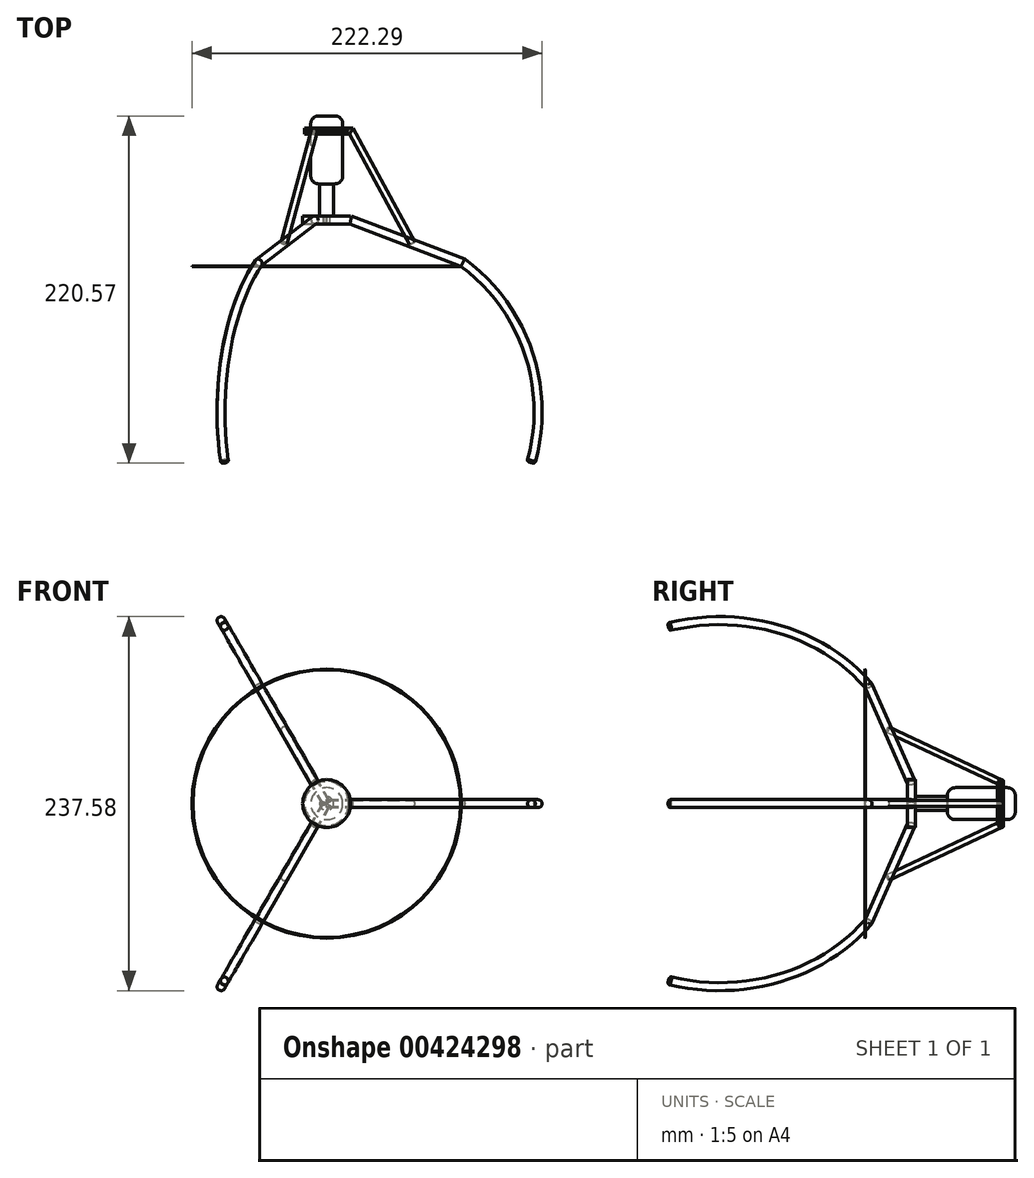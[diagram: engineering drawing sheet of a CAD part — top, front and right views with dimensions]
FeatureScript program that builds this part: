
annotation { "Feature Type Name" : "Feature", "Feature Type Description" : "" }
export const myFeature = defineFeature(function(context is Context, id is Id, definition is map)
    precondition{}
    {
        {
            var Q0;
            Q0=qCreatedBy(makeId("Top.planeOp"),FACE);
            var sketch = newSketch(context, id + "F0", { "sketchPlane" : qUnion([Q0])});
            skLineSegment(sketch, "E0.bottom", {"start": v(15.24, -2.54) * mm, "end": v(-15.24, -2.54) * mm});
            skLineSegment(sketch, "E0.top", {"start": v(15.24, 2.54) * mm, "end": v(-15.24, 2.54) * mm});
            skLineSegment(sketch, "E0.left", {"start": v(15.24, -2.54) * mm, "end": v(15.24, 2.54) * mm});
            skLineSegment(sketch, "E0.right", {"start": v(-15.24, -2.54) * mm, "end": v(-15.24, 2.54) * mm});
            skPoint(sketch, "E0.middle", {"position": v(0, 0) * mm});
            skLineSegment(sketch, "E1.bottom", {"start": v(4.45, 2.54) * mm, "end": v(-4.45, 2.54) * mm});
            skLineSegment(sketch, "E1.top", {"start": v(4.44, 22.86) * mm, "end": v(-4.45, 22.86) * mm});
            skLineSegment(sketch, "E1.left", {"start": v(4.45, 2.54) * mm, "end": v(4.44, 22.86) * mm});
            skLineSegment(sketch, "E1.right", {"start": v(-4.45, 2.54) * mm, "end": v(-4.45, 22.86) * mm});
            skPoint(sketch, "E1.middle", {"position": v(0, 12.7) * mm});
            skLineSegment(sketch, "E2.bottom", {"start": v(0, 22.86) * mm, "end": v(10.16, 22.86) * mm});
            skLineSegment(sketch, "E2.top", {"start": v(0, 66.04) * mm, "end": v(10.16, 66.04) * mm});
            skLineSegment(sketch, "E2.left", {"start": v(0, 22.86) * mm, "end": v(0, 66.04) * mm});
            skLineSegment(sketch, "E2.right", {"start": v(10.16, 22.86) * mm, "end": v(10.16, 66.04) * mm});
            skLineSegment(sketch, "E3.bottom", {"start": v(0, 22.86) * mm, "end": v(-10.16, 22.86) * mm});
            skLineSegment(sketch, "E3.top", {"start": v(0, 66.04) * mm, "end": v(-10.16, 66.04) * mm});
            skLineSegment(sketch, "E3.right", {"start": v(-10.16, 22.86) * mm, "end": v(-10.16, 66.04) * mm});
            skLineSegment(sketch, "E4.bottom", {"start": v(13.97, 54.57) * mm, "end": v(-13.97, 54.57) * mm});
            skLineSegment(sketch, "E4.top", {"start": v(13.97, 58.38) * mm, "end": v(-13.97, 58.38) * mm});
            skLineSegment(sketch, "E4.left", {"start": v(13.97, 54.57) * mm, "end": v(13.97, 58.38) * mm});
            skLineSegment(sketch, "E4.right", {"start": v(-13.97, 54.57) * mm, "end": v(-13.97, 58.38) * mm});
            skPoint(sketch, "E4.middle", {"position": v(0, 56.47) * mm});
            skArc(sketch, "E5", {"start": v(17.88, 57.68) * mm, "mid": v(16.1, 58.97) * mm, "end": v(13.97, 58.38) * mm});
            skArc(sketch, "E6", {"start": v(-13.97, 58.38) * mm, "mid": v(-18.2, 56.47) * mm, "end": v(-13.97, 54.57) * mm});
            skArc(sketch, "E7", {"start": v(16.15, 2.37) * mm, "mid": v(15.7, 2.5) * mm, "end": v(15.24, 2.54) * mm});
            skArc(sketch, "E8", {"start": v(-15.24, 2.54) * mm, "mid": v(-17.78, 0) * mm, "end": v(-15.24, -2.54) * mm});
            skLineSegment(sketch, "E9", {"start": v(17.88, 57.68) * mm, "end": v(56.07, -12.87) * mm});
            skLineSegment(sketch, "E10", {"start": v(13.42, 55.26) * mm, "end": v(48.8, -10.1) * mm});
            skLineSegment(sketch, "E11", {"start": v(16.15, 2.37) * mm, "end": v(48.8, -10.1) * mm});
            skLineSegment(sketch, "E12", {"start": v(14.77, -2.54) * mm, "end": v(85.52, -29.56) * mm});
            skArc(sketch, "E13", {"start": v(84.92, -29.23) * mm, "mid": v(85.2, -29.41) * mm, "end": v(85.52, -29.56) * mm});
            skArc(sketch, "E14", {"start": v(127.93, -151.04) * mm, "mid": v(129.74, -154.14) * mm, "end": v(132.84, -152.33) * mm});
            skArc(sketch, "E15", {"start": v(127.93, -151.04) * mm, "mid": v(125.12, -83.53) * mm, "end": v(84.92, -29.23) * mm});
            skArc(sketch, "E16", {"start": v(132.84, -152.33) * mm, "mid": v(129.91, -81.84) * mm, "end": v(87.93, -25.14) * mm});
            skLineSegment(sketch, "E17", {"start": v(0, -41.5) * mm, "end": v(0, 92.44) * mm});
            skLineSegment(sketch, "E18", {"start": v(44.62, -13.94) * mm, "end": v(59.96, -19.8) * mm});
            skPoint(sketch, "E19.trimOffspring.start.orphan", {"position": v(56.63, -13.94) * mm});
            skArc(sketch, "E20.trimOffspring", {"start": v(87.93, -25.14) * mm, "mid": v(87.65, -24.95) * mm, "end": v(87.33, -24.8) * mm});
            skLineSegment(sketch, "E21.trimOffspring", {"start": v(56.07, -12.87) * mm, "end": v(87.33, -24.8) * mm});
            skLineSegment(sketch, "E22", {"start": v(15.24, 0) * mm, "end": v(86.43, -27.18) * mm});
            skArc(sketch, "E23", {"start": v(129.72, -154.13) * mm, "mid": v(127.94, -83.88) * mm, "end": v(86.43, -27.18) * mm});
            skLineSegment(sketch, "E24", {"start": v(0, 0) * mm, "end": v(15.24, 0) * mm});
            skLineSegment(sketch, "E25", {"start": v(15.65, 56.47) * mm, "end": v(0, 56.47) * mm});
            skLineSegment(sketch, "E26", {"start": v(15.65, 56.47) * mm, "end": v(54.29, -14.9) * mm});
            skSolve(sketch);
        }
        {
            var Q0;
            {var subQ0=sQuery(id+"F0.wireOp",EDGE,"E2.top");Q0=makeQuery(id+"F0.imprint","IMPRINT",FACE,{"disambiguationData":[TD([[makeQuery(id+"F0.imprint","IMPRINT",EDGE,{"derivedFrom":subQ0}),-1.0]])]});}
            var Q1;
            {var subQ0=sQuery(id+"F0.wireOp",EDGE,"E13");var subQ3=sQuery(id+"F0.wireOp",EDGE,"E15");var subQ5=makeQuery(id+"F0.imprint","INTERSECT",VERTEX,{"derivedFrom":[subQ0,subQ3]});Q1=makeQuery(id+"F0.imprint","IMPRINT",FACE,{"disambiguationData":[TD([[makeQuery(id+"F0.imprint","IMPRINT",EDGE,{"disambiguationData":[TD([[subQ5,1.0]])],"derivedFrom":subQ3}),-1.0]])]});}
            var Q2;
            {var subQ5=sQuery(id+"F0.wireOp",EDGE,"E4.left");Q2=makeQuery(id+"F0.imprint","IMPRINT",FACE,{"disambiguationData":[TD([[makeQuery(id+"F0.imprint","IMPRINT",EDGE,{"derivedFrom":subQ5}),1.0]])]});}
            var Q3;
            {var subQ0=sQuery(id+"F0.wireOp",EDGE,"E4.top");var subQ1=sQuery(id+"F0.wireOp",EDGE,"E2.right");var subQ2=makeQuery(id+"F0.imprint","INTERSECT",VERTEX,{"derivedFrom":[subQ1,subQ0]});Q3=makeQuery(id+"F0.imprint","IMPRINT",FACE,{"disambiguationData":[TD([[makeQuery(id+"F0.imprint","IMPRINT",EDGE,{"disambiguationData":[TD([[subQ2,1.0]])],"derivedFrom":subQ1}),1.0]])]});}
            var Q4;
            {var subQ1=sQuery(id+"F0.wireOp",EDGE,"E0.left");Q4=makeQuery(id+"F0.imprint","IMPRINT",FACE,{"disambiguationData":[TD([[makeQuery(id+"F0.imprint","IMPRINT",EDGE,{"derivedFrom":subQ1}),1.0]])]});}
            var Q5;
            {var subQ5=sQuery(id+"F0.wireOp",EDGE,"E2.bottom");var subQ7=makeQuery(id+"F0.imprint","INTERSECT",VERTEX,{"derivedFrom":[sQuery(id+"F0.wireOp",EDGE,"E1.left"),subQ5]});Q5=makeQuery(id+"F0.imprint","IMPRINT",FACE,{"disambiguationData":[TD([[makeQuery(id+"F0.imprint","IMPRINT",EDGE,{"disambiguationData":[TD([[subQ7,-1.0]])],"derivedFrom":subQ5}),1.0]])]});}
            var Q6;
            {var subQ0=sQuery(id+"F0.wireOp",EDGE,"E1.left");Q6=makeQuery(id+"F0.imprint","IMPRINT",FACE,{"disambiguationData":[TD([[makeQuery(id+"F0.imprint","IMPRINT",EDGE,{"derivedFrom":subQ0}),1.0]])]});}
            var Q7;
            Q7=sQuery(id+"F0.wireOp",EDGE,"E17");
            revolve(context, id + "F1", {"entities" : qUnion([Q0, Q1, Q2, Q3, Q4, Q5, Q6]), "axis" : qUnion([Q7]), "revolveType" : RevolveType.FULL});
        }
        {
            var Q0;
            Q0=qCreatedBy(makeId("Right.planeOp"),FACE);
            var sketch = newSketch(context, id + "F2", { "sketchPlane" : qUnion([Q0])});
            skCircle(sketch, "E27", {"center": v(0, 0) * mm, "radius": 2.54 * mm});
            skSolve(sketch);
        }
        {
            var Q0;
            Q0 = qSketchRegion(id + "F2", true);
            var Q1;
            Q1=sQuery(id+"F0.wireOp",EDGE,"E24");
            var Q2;
            Q2=sQuery(id+"F0.wireOp",EDGE,"E22");
            var Q3;
            Q3=sQuery(id+"F0.wireOp",EDGE,"E23");
            sweep(context, id + "F3", {"profiles" : qUnion([Q0]), "path" : qUnion([Q1, Q2, Q3])});
        }
        {
            var Q0;
            Q0=qCreatedBy(makeId("Right.planeOp"),FACE);
            var sketch = newSketch(context, id + "F4", { "sketchPlane" : qUnion([Q0])});
            skLineSegment(sketch, "E28", {"start": v(0, 0) * mm, "end": v(56.52, 0) * mm});
            skCircle(sketch, "E29", {"center": v(56.52, 0) * mm, "radius": 1.9 * mm});
            skSolve(sketch);
        }
        {
            var Q0;
            Q0 = qSketchRegion(id + "F4", true);
            var Q1;
            Q1=sQuery(id+"F0.wireOp",EDGE,"E25");
            var Q2;
            Q2=sQuery(id+"F0.wireOp",EDGE,"E26");
            sweep(context, id + "F5", {"profiles" : qUnion([Q0]), "path" : qUnion([Q1, Q2])});
        }
        {
            var Q0;
            {var subQ6=sQuery(id+"F0.wireOp",EDGE,"E4.right");Q0=makeQuery(id+"F0.imprint","IMPRINT",FACE,{"disambiguationData":[TD([[makeQuery(id+"F0.imprint","IMPRINT",EDGE,{"derivedFrom":subQ6}),-1.0]])]});}
            var Q1;
            {var subQ2=sQuery(id+"F0.wireOp",EDGE,"E4.bottom");var subQ5=sQuery(id+"F0.wireOp",EDGE,"E3.right");var subQ8=makeQuery(id+"F0.imprint","INTERSECT",VERTEX,{"derivedFrom":[subQ5,subQ2]});Q1=makeQuery(id+"F0.imprint","IMPRINT",FACE,{"disambiguationData":[TD([[makeQuery(id+"F0.imprint","IMPRINT",EDGE,{"disambiguationData":[TD([[subQ8,-1.0]])],"derivedFrom":subQ5}),-1.0]])]});}
            var Q2;
            Q2=sQuery(id+"F4.wireOp",EDGE,"E28");
            revolve(context, id + "F6", {"entities" : qUnion([Q0, Q1]), "axis" : qUnion([Q2]), "revolveType" : RevolveType.FULL});
        }
        {
            var Q0;
            Q0=makeQuery(id+"F3.opSweep","SWEPT_BODY",BODY,{"disambiguationData":[OSD([sQuery(id+"F0.wireOp",EDGE,"E23"),sQuery(id+"F2.wireOp",EDGE,"E27")])]});
            var Q1;
            Q1=makeQuery(id+"F5.opSweep","SWEPT_BODY",BODY,{"disambiguationData":[OSD([sQuery(id+"F0.wireOp",EDGE,"E26"),sQuery(id+"F4.wireOp",EDGE,"E29")])]});
            var Q2;
            Q2=sQuery(id+"F0.wireOp",EDGE,"E17");
            circularPattern(context, id + "F7", {"entities" : qUnion([Q0, Q1]), "axis" : qUnion([Q2]), "angle" : 360 * degree, "instanceCount" : 3, "equalSpace" : true});
        }
        {
            var Q0;
            Q0=makeQuery(id+"F3.opSweep","CAP_EDGE",EDGE,{"disambiguationData":[OSD([sQuery(id+"F0.wireOp",VERTEX,"E23.start"),sQuery(id+"F2.wireOp",EDGE,"E27")])],"isStart":false});
            fillet(context, id + "F8", {"entities" : qUnion([Q0]), "radius" : 1.27 * mm, "tangentPropagation" : true, "allowEdgeOverflow" : false});
        }
        {
            var Q0;
            Q0=makeQuery(id+"F7.opPattern","COPY",EDGE,{"derivedFrom":makeQuery(id+"F3.opSweep","CAP_EDGE",EDGE,{"disambiguationData":[OSD([sQuery(id+"F0.wireOp",VERTEX,"E23.start"),sQuery(id+"F2.wireOp",EDGE,"E27")])],"isStart":false}),"instanceName":"1"});
            fillet(context, id + "F9", {"entities" : qUnion([Q0]), "radius" : 1.27 * mm, "tangentPropagation" : true, "allowEdgeOverflow" : false});
        }
        {
            var Q0;
            Q0=makeQuery(id+"F7.opPattern","COPY",EDGE,{"derivedFrom":makeQuery(id+"F3.opSweep","CAP_EDGE",EDGE,{"disambiguationData":[OSD([sQuery(id+"F0.wireOp",VERTEX,"E23.start"),sQuery(id+"F2.wireOp",EDGE,"E27")])],"isStart":false}),"instanceName":"2"});
            fillet(context, id + "F10", {"entities" : qUnion([Q0]), "radius" : 1.27 * mm, "tangentPropagation" : true, "allowEdgeOverflow" : false});
        }
        {
            var Q0;
            Q0=makeQuery(id+"F1.opRevolve","SWEPT_EDGE",EDGE,{"disambiguationData":[OSD([sQuery(id+"F0.wireOp",EDGE,"E2.bottom"),sQuery(id+"F0.wireOp",EDGE,"E2.right")])]});
            fillet(context, id + "F11", {"entities" : qUnion([Q0]), "radius" : 5.08 * mm, "tangentPropagation" : true, "allowEdgeOverflow" : false});
        }
        {
            var Q0;
            Q0=makeQuery(id+"F1.opRevolve","SWEPT_EDGE",EDGE,{"disambiguationData":[OSD([sQuery(id+"F0.wireOp",EDGE,"E2.top"),sQuery(id+"F0.wireOp",EDGE,"E2.right")])]});
            fillet(context, id + "F12", {"entities" : qUnion([Q0]), "radius" : 5.08 * mm, "tangentPropagation" : true, "allowEdgeOverflow" : false});
        }
    });
